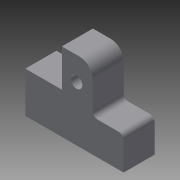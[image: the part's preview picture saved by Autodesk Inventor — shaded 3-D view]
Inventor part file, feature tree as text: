
AUTODESK INVENTOR PART (.ipt)
format: ipt  version: 2015 (Build 190159000, 159)  size: 176,128 bytes
history: native  units: in
note: dims shown in document units (in); Inventor stores cm internally (conversion verified against a paired STEP export)
features: other x7, extrude x7, sketch x7, plane x4, projected_geometry x4, fillet x1
ambient origin geometry x8: Origin, YZ Plane, XZ Plane, XY Plane, X Axis, Y Axis, Z Axis, Center Point
bodies: Body1 (feature_tree)
feature tree (30):
  other  "dc_motor_mount_2012"
  other  "A_2"
  other  "A_3"
  other  "A_4"
  other  "FRONT"
  other  "TOP"
  other  "RIGHT"
  plane  "Work Plane6"
  extrude  "Extrusion1"  Depth=0.5in
  plane  "Work Plane5"
  extrude  "Extrusion2"  Depth=0.5in TaperAngle=0.0deg
  plane  "Work Plane8"
  extrude  "Extrusion3"  Depth=0.3937in TaperAngle=0.0deg
  extrude  "Extrusion4"  Depth=0.0787in
  extrude  "Extrusion5"  Depth=0.3937in
  fillet  "Fillet4"  Radius=0.3937in
  plane  "Work Plane9"
  extrude  "Extrusion6"  [1 undecoded]
  extrude  "Extrusion7"  [1 undecoded]
  sketch  "Sketch1"  dims[d0=0.5in d1=0.0in d2=0.2441in]
  sketch  "Sketch2"  dims[d3=0.5in d4=0.0in d7=0.5in d8=0.0in]
  sketch  "Sketch3"  dims[d12=0.3937in d13=0.0in d14=0.3937in d15=0.0in]
  sketch  "Sketch4"  dims[d16=0.0787in d18=0.1406in]
  projected_geometry  "Projected Loop1"
  sketch  "Sketch5"  dims[d19=0.3937in d20=0.0in d21=0.1406in d22=0.3937in d23=0.0in]
  projected_geometry  "Projected Loop2"
  sketch  "Sketch6"
  projected_geometry  "Projected Loop3"
  sketch  "Sketch7"
  projected_geometry  "Projected Loop4"
note: 2 required parameter values undecoded (feature->parameter linkage not recoverable at this tier; creation-order binding heuristic only, values carry confidence <= 0.55)
